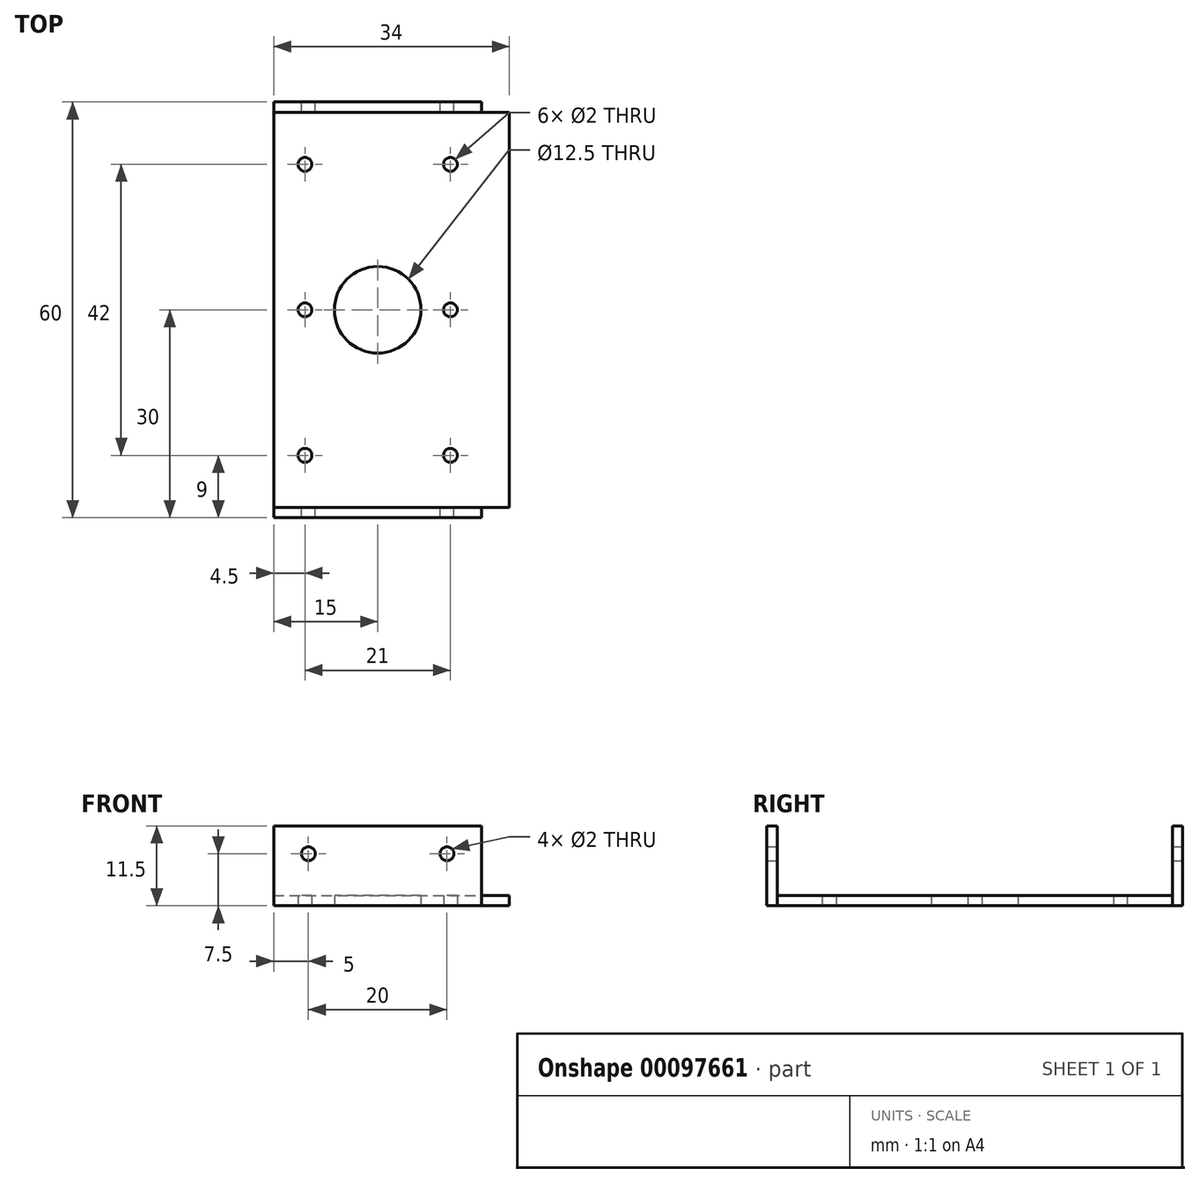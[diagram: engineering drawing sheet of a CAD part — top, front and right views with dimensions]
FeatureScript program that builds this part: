
annotation { "Feature Type Name" : "Feature", "Feature Type Description" : "" }
export const myFeature = defineFeature(function(context is Context, id is Id, definition is map)
    precondition{}
    {
        {
            var Q0;
            Q0=qCreatedBy(makeId("Top.planeOp"),FACE);
            var sketch = newSketch(context, id + "F0", { "sketchPlane" : qUnion([Q0])});
            skLineSegment(sketch, "E0.bottom", {"start": v(-15, -20) * mm, "end": v(15, -20) * mm});
            skLineSegment(sketch, "E0.top", {"start": v(-15, 40) * mm, "end": v(15, 40) * mm});
            skLineSegment(sketch, "E0.left", {"start": v(-15, -20) * mm, "end": v(-15, 40) * mm});
            skLineSegment(sketch, "E0.right", {"start": v(15, -20) * mm, "end": v(15, 40) * mm});
            skLineSegment(sketch, "E1", {"start": v(-15, 10) * mm, "end": v(15, 10) * mm, "construction": true});
            skCircle(sketch, "E2", {"center": v(0, 10) * mm, "radius": 6.25 * mm});
            skCircle(sketch, "E3", {"center": v(10.5, 10) * mm, "radius": 1 * mm});
            skPoint(sketch, "E4", {"position": v(0, -20) * mm});
            skCircle(sketch, "E5", {"center": v(10.5, 31) * mm, "radius": 1 * mm});
            skCircle(sketch, "E6.MirrorC", {"center": v(-10.5, 31) * mm, "radius": 1 * mm});
            skCircle(sketch, "E7.MirrorC", {"center": v(-10.5, 10) * mm, "radius": 1 * mm});
            skCircle(sketch, "E8.MirrorC", {"center": v(-10.5, -11) * mm, "radius": 1 * mm});
            skCircle(sketch, "E9.MirrorC", {"center": v(10.5, -11) * mm, "radius": 1 * mm});
            skSolve(sketch);
        }
        {
            var Q0;
            Q0 = qSketchRegion(id + "F0", true);
            extrude(context, id + "F1", {"entities" : qUnion([Q0]), "depth" : 1.5 * mm});
        }
        {
            var Q0;
            Q0=makeQuery(id+"F1.opExtrude","CAP_FACE",FACE,{"disambiguationData":[OSD([sQuery(id+"F0.wireOp",EDGE,"E0.bottom"),sQuery(id+"F0.wireOp",EDGE,"E0.top"),sQuery(id+"F0.wireOp",EDGE,"E0.left"),sQuery(id+"F0.wireOp",EDGE,"E0.right"),sQuery(id+"F0.wireOp",EDGE,"eqvCYkWH-PHl8-znQ5-vCwl-DDdcap4FGDum"),sQuery(id+"F0.wireOp",EDGE,"lRwWmORh-vMHC-3TIv-xqtC-OO1eycoFhP3Q"),sQuery(id+"F0.wireOp",EDGE,"bYx3IYRZ-9RQz-PRGe-wgUq-1Qj5uMKNi13t"),sQuery(id+"F0.wireOp",EDGE,"f8d3236a-eecd-4399-86dc-6632d9c7c95e0.MirrorC"),sQuery(id+"F0.wireOp",EDGE,"b44e486c-8a70-4c1d-bd86-a08a2f2789f50.MirrorC")])],"isStart":false});
            var sketch = newSketch(context, id + "F2", { "sketchPlane" : qUnion([Q0])});
            skLineSegment(sketch, "E10.bottom", {"start": v(-15, 40) * mm, "end": v(15, 40) * mm});
            skLineSegment(sketch, "E10.top", {"start": v(-15, 38.5) * mm, "end": v(15, 38.5) * mm});
            skLineSegment(sketch, "E10.left", {"start": v(-15, 40) * mm, "end": v(-15, 38.5) * mm});
            skLineSegment(sketch, "E10.right", {"start": v(15, 40) * mm, "end": v(15, 38.5) * mm});
            skLineSegment(sketch, "E11.bottom", {"start": v(-15, -20) * mm, "end": v(15, -20) * mm});
            skLineSegment(sketch, "E11.top", {"start": v(-15, -18.5) * mm, "end": v(15, -18.5) * mm});
            skLineSegment(sketch, "E11.left", {"start": v(-15, -20) * mm, "end": v(-15, -18.5) * mm});
            skLineSegment(sketch, "E11.right", {"start": v(15, -20) * mm, "end": v(15, -18.5) * mm});
            skSolve(sketch);
        }
        {
            var Q0;
            Q0 = qSketchRegion(id + "F2", true);
            extrude(context, id + "F3", {"entities" : qUnion([Q0]), "operationType" : NewBodyOperationType.ADD, "depth" : 10 * mm});
        }
        {
            var Q0;
            Q0=makeQuery(id+"F3.boolean.opBoolean","MERGE",FACE,{"derivedFrom":[makeQuery(id+"F1.opExtrude","SWEPT_FACE",FACE,{"disambiguationData":[OSD([sQuery(id+"F0.wireOp",EDGE,"E0.top")])]}),makeQuery(id+"F3.opExtrude","SWEPT_FACE",FACE,{"disambiguationData":[OSD([sQuery(id+"F2.wireOp",EDGE,"E10.bottom")])]})]});
            var sketch = newSketch(context, id + "F4", { "sketchPlane" : qUnion([Q0])});
            skCircle(sketch, "E12", {"center": v(-10, 7.5) * mm, "radius": 1 * mm});
            skCircle(sketch, "E13.MirrorC", {"center": v(10, 7.5) * mm, "radius": 1 * mm});
            skSolve(sketch);
        }
        {
            var Q0;
            Q0 = qSketchRegion(id + "F4", true);
            extrude(context, id + "F5", {"entities" : qUnion([Q0]), "operationType" : NewBodyOperationType.REMOVE, "endBound" : BoundingType.THROUGH_ALL, "oppositeDirection" : true, "depth" : 25 * mm});
        }
        {
            var Q0;
            Q0=makeQuery(id+"F3.boolean.opBoolean","MERGE",FACE,{"derivedFrom":[makeQuery(id+"F1.opExtrude","SWEPT_FACE",FACE,{"disambiguationData":[OSD([sQuery(id+"F0.wireOp",EDGE,"E0.right")])]}),makeQuery(id+"F3.opExtrude","SWEPT_FACE",FACE,{"disambiguationData":[OSD([sQuery(id+"F2.wireOp",EDGE,"E10.right")])]}),makeQuery(id+"F3.opExtrude","SWEPT_FACE",FACE,{"disambiguationData":[OSD([sQuery(id+"F2.wireOp",EDGE,"E11.right")])]})]});
            var sketch = newSketch(context, id + "F6", { "sketchPlane" : qUnion([Q0])});
            skLineSegment(sketch, "E14.bottom", {"start": v(-18.5, 1.5) * mm, "end": v(38.5, 1.5) * mm});
            skLineSegment(sketch, "E14.top", {"start": v(-18.5, 0) * mm, "end": v(38.5, 0) * mm});
            skLineSegment(sketch, "E14.left", {"start": v(-18.5, 1.5) * mm, "end": v(-18.5, 0) * mm});
            skLineSegment(sketch, "E14.right", {"start": v(38.5, 1.5) * mm, "end": v(38.5, 0) * mm});
            skSolve(sketch);
        }
        {
            var Q0;
            Q0 = qSketchRegion(id + "F6", true);
            extrude(context, id + "F7", {"entities" : qUnion([Q0]), "operationType" : NewBodyOperationType.ADD, "depth" : 4 * mm});
        }
    });
